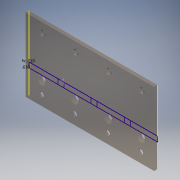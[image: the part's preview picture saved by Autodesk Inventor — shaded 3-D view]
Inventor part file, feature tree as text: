
AUTODESK INVENTOR PART (.ipt)
format: ipt  version: 2019 (Build 230136000, 136)  size: 251,904 bytes
history: native  units: in
note: dims shown in document units (in); Inventor stores cm internally (conversion verified against a paired STEP export)
features: reference x21, other x8, sketch x5, hole x3, extrude x2, chamfer x2, projected_geometry x2, fillet x1
ambient origin geometry x8: Origin, YZ Plane, XZ Plane, XY Plane, X Axis, Y Axis, Z Axis, Center Point
bodies: Solid1 (feature_tree)
feature tree (44):
  extrude  "Extrusion1"  Depth=4.85in
  hole  "Hole1"  [1 undecoded]
  hole  "Hole2"  [1 undecoded]
  hole  "Hole3"  [1 undecoded]
  extrude  "Extrusion2"  Depth=0.125in
  fillet  "Fillet1"  Radius=0.01in
  chamfer  "Chamfer1"  Distance=0.01in
  chamfer  "Chamfer2"  Distance=0.01in
  sketch  "Sketch1"  dims[d0=2.75in d1=4.85in]
  sketch  "Sketch2"  dims[d2=0.125in d3=0.0in d5=0.385in]
  sketch  "Sketch3"  dims[d6=0.6in d7=1.25in]
  projected_geometry  "Projected Loop1"
  sketch  "Sketch4"  dims[d8=1.25in d9=1.25in]
  projected_geometry  "Projected Loop2"
  sketch  "Sketch5"  dims[d10=0.177in d11=0.75in d12=0.385in d13=0.25in d14=0.5635in d15=1.0in d16=0.8108in d19=0.177in d20=1.717in d21=0.332in d22=0.25in d23=0.5635in d24=1.0in d25=0.8108in d26=2.0in d27=0.177in d28=1.717in d29=0.332in d30=0.25in d31=0.5635in d32=1.0in d33=0.8108in d34=0.01in d35=0.01in d36=0.01in d37=0.01in d38=0.01in d39=0.01in d40=0.01in d41=0.01in d42=0.2in d43=0.0in d44=0.01in d45=0.01in d46=0.005in d47=0.1in d48=0.125in d49=0.095in d50=45.0deg d51=0.125in d52=0.095in d53=45.0deg]
  reference  "Reference1"
  reference  "Reference2"
  reference  "Reference3"
  reference  "Reference4"
  reference  "Reference5"
  reference  "Reference6"
  reference  "Reference7"
  reference  "Reference8"
  reference  "Reference9"
  reference  "Reference10"
  reference  "Reference11"
  reference  "Reference12"
  reference  "Reference13"
  reference  "Reference14"
  reference  "Reference15"
  reference  "Reference16"
  reference  "Reference17"
  reference  "Reference18"
  reference  "Reference19"
  reference  "Reference20"
  reference  "Reference21"
  parser-record x1  (decoder bookkeeping rows leaked as tree rows — omitted from the tree; the rows remain in map.json)
  other  "talon stack.iam"
  other  "Victor_SPX_217-9191:3"
  other  "217-9191-001 Rev3_1"
  other  "Victor_SPX_217-9191:4"
  other  "Victor_SPX_217-9191:2"
  other  "217-9191-002 Rev3_2"
  other  "Victor_SPX_217-9191:1"
note: 3 required parameter values undecoded (feature->parameter linkage not recoverable at this tier; creation-order binding heuristic only, values carry confidence <= 0.55)
note: 1 file-system path scrubbed to <path> (originals preserved in map.json)
